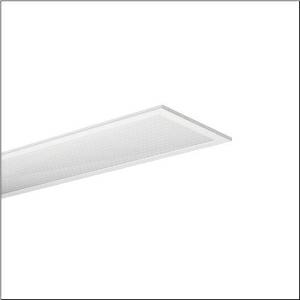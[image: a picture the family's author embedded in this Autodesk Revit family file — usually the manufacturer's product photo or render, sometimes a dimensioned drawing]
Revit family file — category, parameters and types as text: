
# Revit family: apollon_21_linear_51mq18wd2412
name_source: partatom
category: Lighting Fixtures
units: mm (PartAtom-declared; Revit-internal decimal feet)

## family parameters
Cut with Voids When Loaded = No
Host = Face
Light Source = No
Part Type = Normal
Room Calculation Point = No
Round Connector Dimension = Use Diameter
Shared = No

## types (1)
- Apollon 21 linear (1 x LED, 4000 lm, 33 W, 4000K)
    Apparent Load = 33 VA
    CIE Flux Codes = 60 89 97 100 100
    Color Rendering = 80
    Color Temperature = 4000K
    Default Elevation = 1800 mm
    Description = Apollon 21 linear, office luminaire, primary optical cover: micro prismatic cover, CAT 2 (L<= 3000cd/m²), light emission: direct distribution, primary light characteristic: symmetric, installation type: lay-in mounting, LED, rated luminous flux: 4.000lm, luminous efficacy: 121lm/W, light colour: 840, colour temperature: 4000K, control gear: DALI, with terminal, 5-pole, mains connection: 220..240V, AC, 50/60Hz, rated input power: 33W, housing, of aluminium, coated, pure white, module: M600, length: 1.195mm, width: 295mm, height: 39mm, housing upper side, of sheet steel, galvanised, protection rating (complete): IP20, protection rating (lamp compartment, on room side): IP50, insulation class (complete): insulation class II (safety insulation), certification: CE, ENEC, packaging unit: 1 piece
    Height = 0 mm  [stored 0 ft]
    Lamp = 1 x LED
    Lamp Light Flux = 4000 lm
    Lamp Power = 33 W
    Lamp count = 1
    Length = 1195 mm
    Luminous efficacy = 121 lm/W
    Manufacturer = Siteco
    ModVariant = No
    Model = 51MQ18WD2412
    Mounting Place = Ceiling
    Mounting Type = Recessed
    Number of Poles = 1
    OnlyDefault = Yes
    Power Factor = 1
    Product Name = Apollon 21 linear
    Product group = office luminaire | ceiling recessed
    ProductGroupID = 400
    Protection Class = Protection class II
    Protection Degree = IP 20
    RLX_Detail_Level = 1
    RLX_Emergency_Light_Flux = 0 lm
    RLX_Emergency_Type = 0
    RLX_Emergency_Type_DB = No
    RlxData = <blob elided: 15041 chars, md5=645fc01f>
    Socket = socket
    Standby Power = 0 W
    System Light Flux = 4000 lm
    System Power = 33 W
    Type Comments = Product without accessories
    Type Image = l_1291045.jpg
    URL = http://relux.com
    VarID = ---
    Voltage = 0 V
    Weight = 0.00 kg
    Width = 295 mm

note: [stored X ft] marks values corroborated as IEEE doubles in the binary element streams (Revit-internal decimal feet)

## geometry (parser evidence)
native form markers: Sweep x9
no freeform markers — native parametric forms only
